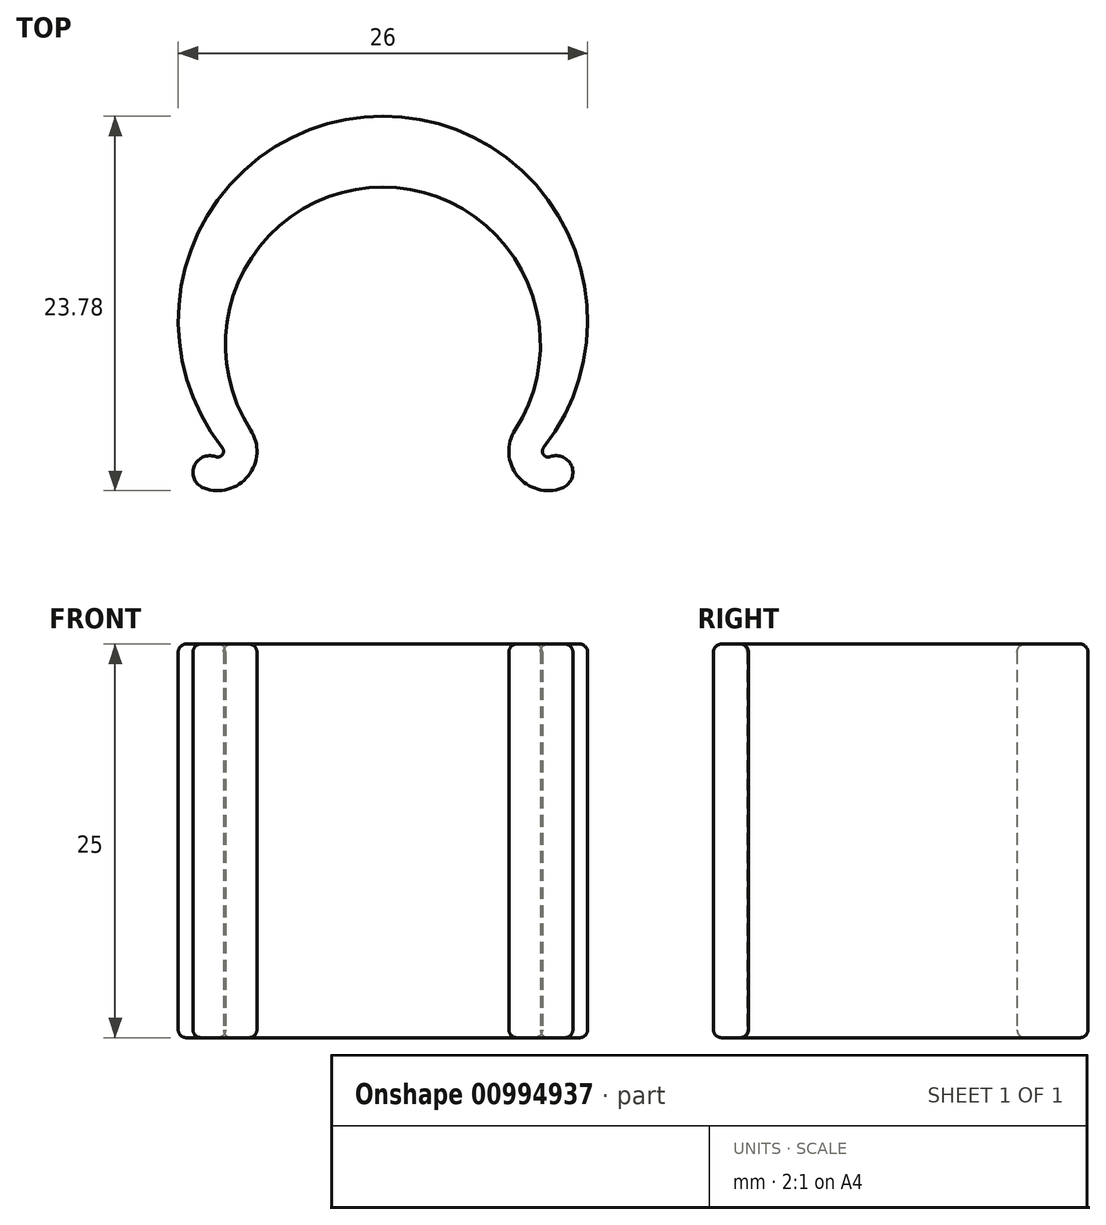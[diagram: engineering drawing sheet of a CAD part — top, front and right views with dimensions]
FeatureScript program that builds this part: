
annotation { "Feature Type Name" : "Feature", "Feature Type Description" : "" }
export const myFeature = defineFeature(function(context is Context, id is Id, definition is map)
    precondition{}
    {
        {
            var Q0;
            Q0=qCreatedBy(makeId("Top.planeOp"),FACE);
            var sketch = newSketch(context, id + "F0", { "sketchPlane" : qUnion([Q0])});
            skPoint(sketch, "E0.second.point", {"position": v(-59.9, -66.27) * mm});
            skArc(sketch, "E1", {"start": v(-59.9, -64.76) * mm, "mid": v(-60.66, -65.51) * mm, "end": v(-59.9, -66.27) * mm});
            skPoint(sketch, "E1.first.point", {"position": v(-59.9, -64.76) * mm});
            skPoint(sketch, "E1.third.point", {"position": v(-59.4, -64.94) * mm});
            skArc(sketch, "E2.MirrorCS", {"start": v(59.9, -64.76) * mm, "mid": v(60.66, -65.51) * mm, "end": v(59.9, -66.27) * mm});
            skPoint(sketch, "E3.MirrorP", {"position": v(59.9, -64.76) * mm});
            skPoint(sketch, "E4.MirrorP", {"position": v(59.9, -66.27) * mm});
            skPoint(sketch, "E5.MirrorP", {"position": v(59.4, -64.94) * mm});
            skArc(sketch, "E6", {"start": v(0, 10) * mm, "mid": v(-8.78, 4.78) * mm, "end": v(-8.4, -5.43) * mm});
            skArc(sketch, "E7", {"start": v(0, 14.5) * mm, "mid": v(-11.7, 7.17) * mm, "end": v(-10.2, -6.55) * mm});
            skLineSegment(sketch, "E8", {"start": v(0, 21.68) * mm, "end": v(0, -12.2) * mm, "construction": true});
            skArc(sketch, "E9", {"start": v(-11.37, -9.13) * mm, "mid": v(-8.55, -8.35) * mm, "end": v(-8.4, -5.43) * mm});
            skArc(sketch, "E10", {"start": v(-10.63, -7.13) * mm, "mid": v(-10.2, -7) * mm, "end": v(-10.2, -6.55) * mm});
            skArc(sketch, "E11", {"start": v(-10.63, -7.13) * mm, "mid": v(-12, -7.76) * mm, "end": v(-11.37, -9.13) * mm});
            skPoint(sketch, "E11.first.point", {"position": v(-10.63, -7.13) * mm});
            skPoint(sketch, "E11.second.point", {"position": v(-11.37, -9.13) * mm});
            skArc(sketch, "E12.MirrorCS", {"start": v(10.63, -7.13) * mm, "mid": v(12, -7.76) * mm, "end": v(11.37, -9.13) * mm});
            skArc(sketch, "E13.MirrorCS", {"start": v(10.63, -7.13) * mm, "mid": v(10.2, -7) * mm, "end": v(10.2, -6.55) * mm});
            skArc(sketch, "E14.MirrorCS", {"start": v(11.37, -9.13) * mm, "mid": v(8.55, -8.35) * mm, "end": v(8.4, -5.43) * mm});
            skPoint(sketch, "E15.MirrorP", {"position": v(11.37, -9.13) * mm});
            skArc(sketch, "E16.MirrorCS", {"start": v(0, 10) * mm, "mid": v(8.78, 4.78) * mm, "end": v(8.4, -5.43) * mm});
            skPoint(sketch, "E17.MirrorP", {"position": v(10.63, -7.13) * mm});
            skArc(sketch, "E18.MirrorCS", {"start": v(0, 14.5) * mm, "mid": v(11.7, 7.17) * mm, "end": v(10.2, -6.55) * mm});
            skSolve(sketch);
        }
        {
            var Q0;
            Q0=makeQuery(id+"F0.imprint","IMPRINT",FACE,{"disambiguationData":[TD([[makeQuery(id+"F0.imprint","IMPRINT",EDGE,{"derivedFrom":sQuery(id+"F0.wireOp",EDGE,"E6")}),-1.0]])]});
            extrude(context, id + "F1", {"entities" : qUnion([Q0]), "flatOperationType" : FlatOperationType.REMOVE, "depth" : 25 * mm, "offsetDistance" : 25 * mm, "domain" : OperationDomain.MODEL, "symmetric" : true});
        }
        {
            var Q0;
            Q0=makeQuery(id+"F1.opExtrude","CAP_EDGE",EDGE,{"disambiguationData":[OSD([sQuery(id+"F0.wireOp",EDGE,"E9")])],"isStart":false});
            var Q1;
            Q1=makeQuery(id+"F1.opExtrude","SWEPT_EDGE",EDGE,{"disambiguationData":[OSD([sQuery(id+"F0.wireOp",EDGE,"E6"),sQuery(id+"F0.wireOp",EDGE,"E9")])]});
            var Q2;
            Q2=makeQuery(id+"F1.opExtrude","CAP_FACE",FACE,{"disambiguationData":[OSD([sQuery(id+"F0.wireOp",EDGE,"E6"),sQuery(id+"F0.wireOp",EDGE,"E7"),sQuery(id+"F0.wireOp",EDGE,"E9"),sQuery(id+"F0.wireOp",EDGE,"E10"),sQuery(id+"F0.wireOp",EDGE,"E11"),sQuery(id+"F0.wireOp",EDGE,"E12.MirrorCS"),sQuery(id+"F0.wireOp",EDGE,"E13.MirrorCS"),sQuery(id+"F0.wireOp",EDGE,"E14.MirrorCS"),sQuery(id+"F0.wireOp",EDGE,"E16.MirrorCS"),sQuery(id+"F0.wireOp",EDGE,"E18.MirrorCS")])],"isStart":true});
            var Q3;
            Q3=makeQuery(id+"F1.opExtrude","CAP_FACE",FACE,{"disambiguationData":[OSD([sQuery(id+"F0.wireOp",EDGE,"E6"),sQuery(id+"F0.wireOp",EDGE,"E7"),sQuery(id+"F0.wireOp",EDGE,"E9"),sQuery(id+"F0.wireOp",EDGE,"E10"),sQuery(id+"F0.wireOp",EDGE,"E11"),sQuery(id+"F0.wireOp",EDGE,"E12.MirrorCS"),sQuery(id+"F0.wireOp",EDGE,"E13.MirrorCS"),sQuery(id+"F0.wireOp",EDGE,"E14.MirrorCS"),sQuery(id+"F0.wireOp",EDGE,"E16.MirrorCS"),sQuery(id+"F0.wireOp",EDGE,"E18.MirrorCS")])],"isStart":false});
            var Q4;
            Q4=makeQuery(id+"F1.opExtrude","SWEPT_FACE",FACE,{"disambiguationData":[OSD([sQuery(id+"F0.wireOp",EDGE,"E6"),sQuery(id+"F0.wireOp",EDGE,"E16.MirrorCS")])]});
            var Q5;
            Q5=makeQuery(id+"F1.opExtrude","SWEPT_FACE",FACE,{"disambiguationData":[OSD([sQuery(id+"F0.wireOp",EDGE,"E7"),sQuery(id+"F0.wireOp",EDGE,"E18.MirrorCS")])]});
            var Q6;
            Q6=makeQuery(id+"F1.opExtrude","SWEPT_FACE",FACE,{"disambiguationData":[OSD([sQuery(id+"F0.wireOp",EDGE,"E9")])]});
            var Q7;
            Q7=makeQuery(id+"F1.opExtrude","SWEPT_FACE",FACE,{"disambiguationData":[OSD([sQuery(id+"F0.wireOp",EDGE,"E10")])]});
            var Q8;
            Q8=makeQuery(id+"F1.opExtrude","SWEPT_FACE",FACE,{"disambiguationData":[OSD([sQuery(id+"F0.wireOp",EDGE,"E12.MirrorCS")])]});
            var Q9;
            Q9=makeQuery(id+"F1.opExtrude","SWEPT_FACE",FACE,{"disambiguationData":[OSD([sQuery(id+"F0.wireOp",EDGE,"E13.MirrorCS")])]});
            var Q10;
            Q10=makeQuery(id+"F1.opExtrude","CAP_EDGE",EDGE,{"disambiguationData":[OSD([sQuery(id+"F0.wireOp",EDGE,"E6"),sQuery(id+"F0.wireOp",EDGE,"E16.MirrorCS")])],"isStart":false});
            var Q11;
            Q11=makeQuery(id+"F1.opExtrude","SWEPT_FACE",FACE,{"disambiguationData":[OSD([sQuery(id+"F0.wireOp",EDGE,"E14.MirrorCS")])]});
            var Q12;
            Q12=makeQuery(id+"F1.opExtrude","CAP_EDGE",EDGE,{"disambiguationData":[OSD([sQuery(id+"F0.wireOp",EDGE,"E7"),sQuery(id+"F0.wireOp",EDGE,"E18.MirrorCS")])],"isStart":true});
            var Q13;
            Q13=makeQuery(id+"F1.opExtrude","CAP_EDGE",EDGE,{"disambiguationData":[OSD([sQuery(id+"F0.wireOp",EDGE,"E7"),sQuery(id+"F0.wireOp",EDGE,"E18.MirrorCS")])],"isStart":false});
            var Q14;
            Q14=makeQuery(id+"F1.opExtrude","CAP_EDGE",EDGE,{"disambiguationData":[OSD([sQuery(id+"F0.wireOp",EDGE,"E9")])],"isStart":true});
            var Q15;
            Q15=makeQuery(id+"F1.opExtrude","CAP_EDGE",EDGE,{"disambiguationData":[OSD([sQuery(id+"F0.wireOp",EDGE,"E11")])],"isStart":false});
            var Q16;
            Q16=makeQuery(id+"F1.opExtrude","CAP_EDGE",EDGE,{"disambiguationData":[OSD([sQuery(id+"F0.wireOp",EDGE,"E13.MirrorCS")])],"isStart":false});
            var Q17;
            Q17=makeQuery(id+"F1.opExtrude","CAP_EDGE",EDGE,{"disambiguationData":[OSD([sQuery(id+"F0.wireOp",EDGE,"E10")])],"isStart":false});
            var Q18;
            Q18=makeQuery(id+"F1.opExtrude","SWEPT_EDGE",EDGE,{"disambiguationData":[OSD([sQuery(id+"F0.wireOp",EDGE,"E7"),sQuery(id+"F0.wireOp",EDGE,"E10")])]});
            var Q19;
            Q19=makeQuery(id+"F1.opExtrude","SWEPT_EDGE",EDGE,{"disambiguationData":[OSD([sQuery(id+"F0.wireOp",EDGE,"E9"),sQuery(id+"F0.wireOp",EDGE,"E11")])]});
            var Q20;
            Q20=makeQuery(id+"F1.opExtrude","SWEPT_EDGE",EDGE,{"disambiguationData":[OSD([sQuery(id+"F0.wireOp",EDGE,"E12.MirrorCS"),sQuery(id+"F0.wireOp",EDGE,"E13.MirrorCS")])]});
            var Q21;
            Q21=makeQuery(id+"F1.opExtrude","SWEPT_EDGE",EDGE,{"disambiguationData":[OSD([sQuery(id+"F0.wireOp",EDGE,"E12.MirrorCS"),sQuery(id+"F0.wireOp",EDGE,"E14.MirrorCS")])]});
            var Q22;
            Q22=makeQuery(id+"F1.opExtrude","SWEPT_EDGE",EDGE,{"disambiguationData":[OSD([sQuery(id+"F0.wireOp",EDGE,"E13.MirrorCS"),sQuery(id+"F0.wireOp",EDGE,"E18.MirrorCS")])]});
            var Q23;
            Q23=makeQuery(id+"F1.opExtrude","SWEPT_FACE",FACE,{"disambiguationData":[OSD([sQuery(id+"F0.wireOp",EDGE,"E11")])]});
            var Q24;
            Q24=makeQuery(id+"F1.opExtrude","SWEPT_EDGE",EDGE,{"disambiguationData":[OSD([sQuery(id+"F0.wireOp",EDGE,"E14.MirrorCS"),sQuery(id+"F0.wireOp",EDGE,"E16.MirrorCS")])]});
            var Q25;
            Q25=makeQuery(id+"F1.opExtrude","CAP_EDGE",EDGE,{"disambiguationData":[OSD([sQuery(id+"F0.wireOp",EDGE,"E6"),sQuery(id+"F0.wireOp",EDGE,"E16.MirrorCS")])],"isStart":true});
            var Q26;
            Q26=makeQuery(id+"F1.opExtrude","CAP_EDGE",EDGE,{"disambiguationData":[OSD([sQuery(id+"F0.wireOp",EDGE,"E12.MirrorCS")])],"isStart":true});
            var Q27;
            Q27=makeQuery(id+"F1.opExtrude","CAP_EDGE",EDGE,{"disambiguationData":[OSD([sQuery(id+"F0.wireOp",EDGE,"E12.MirrorCS")])],"isStart":false});
            var Q28;
            Q28=makeQuery(id+"F1.opExtrude","CAP_EDGE",EDGE,{"disambiguationData":[OSD([sQuery(id+"F0.wireOp",EDGE,"E13.MirrorCS")])],"isStart":true});
            var Q29;
            Q29=makeQuery(id+"F1.opExtrude","CAP_EDGE",EDGE,{"disambiguationData":[OSD([sQuery(id+"F0.wireOp",EDGE,"E14.MirrorCS")])],"isStart":true});
            var Q30;
            Q30=makeQuery(id+"F1.opExtrude","CAP_EDGE",EDGE,{"disambiguationData":[OSD([sQuery(id+"F0.wireOp",EDGE,"E14.MirrorCS")])],"isStart":false});
            var Q31;
            Q31=makeQuery(id+"F1.opExtrude","CAP_EDGE",EDGE,{"disambiguationData":[OSD([sQuery(id+"F0.wireOp",EDGE,"E10")])],"isStart":true});
            var Q32;
            Q32=makeQuery(id+"F1.opExtrude","SWEPT_EDGE",EDGE,{"disambiguationData":[OSD([sQuery(id+"F0.wireOp",EDGE,"E10"),sQuery(id+"F0.wireOp",EDGE,"E11")])]});
            var Q33;
            Q33=makeQuery(id+"F1.opExtrude","CAP_EDGE",EDGE,{"disambiguationData":[OSD([sQuery(id+"F0.wireOp",EDGE,"E11")])],"isStart":true});
            fillet(context, id + "F2", {"entities" : qUnion([Q0, Q1, Q2, Q3, Q4, Q5, Q6, Q7, Q8, Q9, Q10, Q11, Q12, Q13, Q14, Q15, Q16, Q17, Q18, Q19, Q20, Q21, Q22, Q23, Q24, Q25, Q26, Q27, Q28, Q29, Q30, Q31, Q32, Q33]), "radius" : 0.5 * mm, "tangentPropagation" : true, "allowEdgeOverflow" : false});
        }
    });
